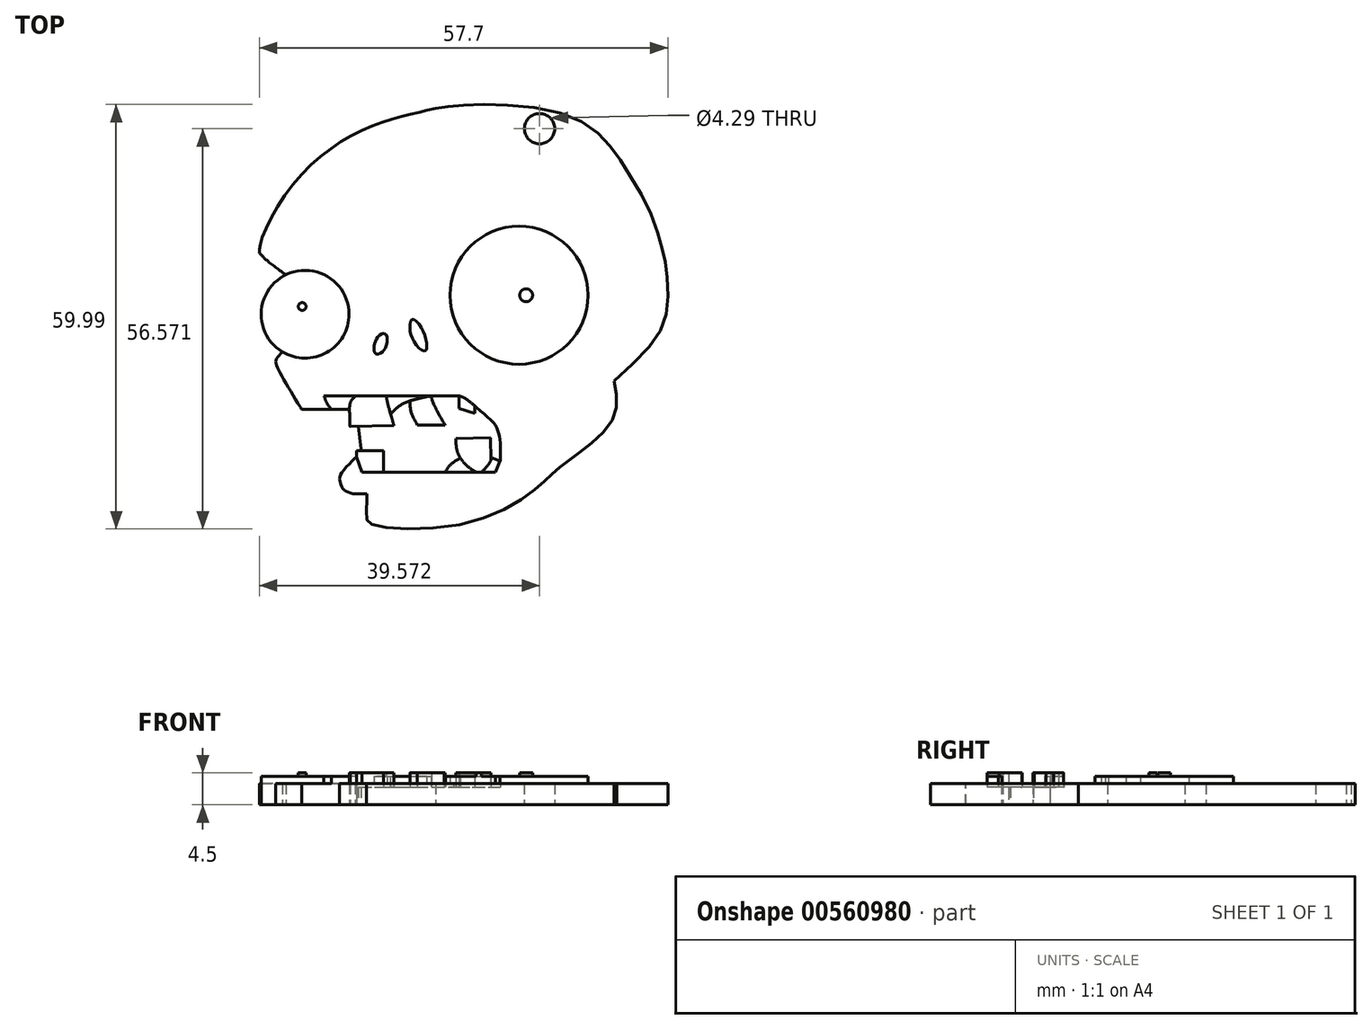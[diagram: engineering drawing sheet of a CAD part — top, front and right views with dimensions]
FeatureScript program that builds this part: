
annotation { "Feature Type Name" : "Feature", "Feature Type Description" : "" }
export const myFeature = defineFeature(function(context is Context, id is Id, definition is map)
    precondition{}
    {
        {
            var Q0;
            Q0=qCreatedBy(makeId("Top.planeOp"),FACE);
            var sketch = newSketch(context, id + "F0", { "sketchPlane" : qUnion([Q0])});
            skCircle(sketch, "E0", {"center": v(10.55, 3.84) * mm, "radius": 9.76 * mm});
            skFitSpline(sketch, "E1", {"points": [v(-1.24, 30.23) * mm, v(-6.33, 29.03) * mm, v(-13.62, 26.14) * mm, v(-21.9, 18.85) * mm, v(-26, 11.16) * mm, v(-26.1, 9.77) * mm], "startDerivative": vector(-26.84, -5.7) * mm, "endDerivative": vector(0.99, -11.94) * mm});
            skFitSpline(sketch, "E2", {"points": [v(-1.24, 30.23) * mm, v(1.46, 30.62) * mm, v(7.78, 30.76) * mm, v(17.95, 29.1) * mm, v(22.92, 25.53) * mm, v(25.72, 21.6) * mm, v(29.16, 15.43) * mm, v(30.75, 10.4) * mm, v(31.36, 7.6) * mm, v(31.5, 2.45) * mm, v(29.95, -2.13) * mm, v(23.95, -8.27) * mm], "startDerivative": vector(39.01, 6.86) * mm, "endDerivative": vector(-62.58, -55.62) * mm});
            skFitSpline(sketch, "E3", {"points": [v(23.95, -8.27) * mm, v(23.95, -13.29) * mm, v(19.3, -18.23) * mm, v(15.84, -20.84) * mm, v(13.3, -23.17) * mm, v(3.06, -28.39) * mm, v(-10.49, -28.46) * mm, v(-10.98, -27.33) * mm, v(-10.95, -24.36) * mm, v(-10.95, -24.15) * mm], "startDerivative": vector(8.57, -43.63) * mm, "endDerivative": vector(-0.07, 5.38) * mm});
            skFitSpline(sketch, "E4", {"points": [v(-10.95, -24.2) * mm, v(-12.88, -24.2) * mm, v(-14.3, -23.56) * mm, v(-14.7, -22.64) * mm, v(-14.75, -21.75) * mm, v(-12.59, -19.14) * mm], "startDerivative": vector(-8.99, -0.7) * mm, "endDerivative": vector(10.21, 10.19) * mm});
            skCircle(sketch, "E5", {"center": v(-19.68, 1.16) * mm, "radius": 6.2 * mm});
            skFitSpline(sketch, "E6", {"points": [v(-26.1, 9.77) * mm, v(-25.04, 8.74) * mm, v(-22.4, 6.73) * mm], "startDerivative": vector(2.28, -2.41) * mm, "endDerivative": vector(4.94, -3.58) * mm});
            skFitSpline(sketch, "E7", {"points": [v(-22.87, -4.17) * mm, v(-23.73, -5.16) * mm, v(-23.75, -5.96) * mm, v(-22.45, -8.5) * mm, v(-20.25, -12.15) * mm, v(-20.14, -12.3) * mm], "startDerivative": vector(-5.77, -5.5) * mm, "endDerivative": vector(1.02, -1.28) * mm});
            skLineSegment(sketch, "E8", {"start": v(-20.14, -12.3) * mm, "end": v(-15.94, -12.3) * mm});
            skFitSpline(sketch, "E9", {"points": [v(-12.5, -10.36) * mm, v(-13.26, -11.26) * mm, v(-13.38, -12.96) * mm, v(-13.31, -14.7) * mm, v(-13.3, -14.7) * mm], "startDerivative": vector(-3.23, -2.9) * mm, "endDerivative": vector(0.53, 0.26) * mm});
            skLineSegment(sketch, "E10", {"start": v(-13.3, -14.7) * mm, "end": v(-7.12, -14.56) * mm});
            skLineSegment(sketch, "E11", {"start": v(-12.5, -10.36) * mm, "end": v(-8.21, -10.36) * mm});
            skFitSpline(sketch, "E12", {"points": [v(-8.21, -10.36) * mm, v(-7.98, -11.5) * mm, v(-7.12, -14.56) * mm], "startDerivative": vector(0.46, -2.68) * mm, "endDerivative": vector(1.63, -5.49) * mm});
            skFitSpline(sketch, "E13", {"points": [v(-15.94, -12.3) * mm, v(-16.54, -11.5) * mm, v(-17.02, -10.36) * mm], "startDerivative": vector(-1.36, 1.54) * mm, "endDerivative": vector(-0.8, 2.3) * mm});
            skLineSegment(sketch, "E14", {"start": v(-17.02, -10.36) * mm, "end": v(-12.5, -10.36) * mm});
            skLineSegment(sketch, "E15", {"start": v(-15.94, -12.3) * mm, "end": v(-13.4, -12.3) * mm});
            skLineSegment(sketch, "E16", {"start": v(-8.21, -10.36) * mm, "end": v(-1.77, -10.36) * mm});
            skFitSpline(sketch, "E17", {"points": [v(-7.59, -12.96) * mm, v(-5.88, -11.5) * mm, v(-1.77, -10.36) * mm], "startDerivative": vector(3.41, 3.77) * mm, "endDerivative": vector(7.97, 1.55) * mm});
            skLineSegment(sketch, "E18", {"start": v(-3.8, -14.5) * mm, "end": v(0, -14.5) * mm});
            skLineSegment(sketch, "E19", {"start": v(0, -14.5) * mm, "end": v(0.1, -14.54) * mm});
            skFitSpline(sketch, "E20", {"points": [v(-4.86, -11.08) * mm, v(-4.71, -12.6) * mm, v(-3.8, -14.5) * mm], "startDerivative": vector(0, -3.23) * mm, "endDerivative": vector(2.04, -3.57) * mm});
            skFitSpline(sketch, "E21", {"points": [v(-1.77, -10.36) * mm, v(-1.77, -10.82) * mm, v(0.1, -14.54) * mm], "startDerivative": vector(-0.3, -1.44) * mm, "endDerivative": vector(3.42, -6.13) * mm});
            skLineSegment(sketch, "E22", {"start": v(2.07, -10.66) * mm, "end": v(2.07, -12.17) * mm});
            skLineSegment(sketch, "E23", {"start": v(2.07, -12.17) * mm, "end": v(1.98, -12.17) * mm});
            skLineSegment(sketch, "E24", {"start": v(4.28, -11.78) * mm, "end": v(4.28, -12.88) * mm});
            skLineSegment(sketch, "E25", {"start": v(2.07, -12.17) * mm, "end": v(4.28, -12.88) * mm});
            skLineSegment(sketch, "E26", {"start": v(-1.77, -10.36) * mm, "end": v(1.33, -10.36) * mm});
            skFitSpline(sketch, "E27", {"points": [v(1.33, -10.36) * mm, v(2.45, -10.5) * mm, v(4.28, -11.78) * mm], "startDerivative": vector(2.61, 0.08) * mm, "endDerivative": vector(3.26, -2.76) * mm});
            skLineSegment(sketch, "E28", {"start": v(2.07, -10.66) * mm, "end": v(2.07, -10.39) * mm});
            skFitSpline(sketch, "E29", {"points": [v(-4.58, 0.44) * mm, v(-3.8, 0) * mm, v(-2.71, -1.93) * mm, v(-2.49, -3.58) * mm, v(-2.69, -3.98) * mm, v(-3.36, -3.85) * mm, v(-4.53, -2.13) * mm, v(-4.88, -0.86) * mm, v(-4.58, 0.44) * mm]});
            skFitSpline(sketch, "E30", {"points": [v(-9.62, -2.38) * mm, v(-8.97, -1.68) * mm, v(-8.52, -1.55) * mm, v(-8.17, -1.8) * mm, v(-8.1, -2.78) * mm, v(-8.45, -3.85) * mm, v(-9.07, -4.37) * mm, v(-9.65, -4.45) * mm, v(-9.92, -3.95) * mm, v(-9.87, -3.18) * mm, v(-9.62, -2.38) * mm]});
            skFitSpline(sketch, "E31", {"points": [v(-12.15, -14.68) * mm, v(-11.76, -17.9) * mm], "startDerivative": vector(0.39, -3.22) * mm, "endDerivative": vector(0.39, -3.22) * mm});
            skLineSegment(sketch, "E32", {"start": v(-12.01, -21.18) * mm, "end": v(7.22, -21.18) * mm});
            skLineSegment(sketch, "E33", {"start": v(1.61, -16.41) * mm, "end": v(6.5, -16.26) * mm});
            skLineSegment(sketch, "E34", {"start": v(6.5, -16.26) * mm, "end": v(6.6, -19.46) * mm});
            skFitSpline(sketch, "E35", {"points": [v(1.61, -16.41) * mm, v(1.89, -18.38) * mm, v(3.09, -20.16) * mm, v(4.51, -21.18) * mm], "startDerivative": vector(0.2, -5.94) * mm, "endDerivative": vector(4.63, -2.79) * mm});
            skFitSpline(sketch, "E36", {"points": [v(6.6, -19.46) * mm, v(6.11, -20.24) * mm, v(5.24, -21.18) * mm], "startDerivative": vector(-0.93, -1.68) * mm, "endDerivative": vector(-1.76, -1.74) * mm});
            skFitSpline(sketch, "E37", {"points": [v(2.27, -19.16) * mm, v(0.83, -20.15) * mm, v(0.15, -21.18) * mm], "startDerivative": vector(-2.96, -1.7) * mm, "endDerivative": vector(-1.23, -2.35) * mm});
            skFitSpline(sketch, "E38", {"points": [v(6.59, -19.1) * mm, v(7.66, -19.51) * mm, v(7.9, -19.62) * mm], "startDerivative": vector(1.87, -0.72) * mm, "endDerivative": vector(0.63, -0.27) * mm});
            skLineSegment(sketch, "E39", {"start": v(-11.76, -17.9) * mm, "end": v(-11.76, -18.13) * mm});
            skLineSegment(sketch, "E40", {"start": v(-11.76, -18.13) * mm, "end": v(-8.63, -18.13) * mm});
            skLineSegment(sketch, "E41", {"start": v(-8.63, -18.13) * mm, "end": v(-8.63, -21.18) * mm});
            skLineSegment(sketch, "E42", {"start": v(-11.76, -18.13) * mm, "end": v(-12.42, -18.13) * mm});
            skLineSegment(sketch, "E43", {"start": v(-12.42, -18.13) * mm, "end": v(-12.42, -19) * mm});
            skLineSegment(sketch, "E44", {"start": v(-12.42, -19) * mm, "end": v(-12.59, -19.14) * mm});
            skLineSegment(sketch, "E45", {"start": v(-12.42, -19) * mm, "end": v(-11.62, -21.18) * mm});
            skFitSpline(sketch, "E46", {"points": [v(4.28, -11.78) * mm, v(5.6, -12.93) * mm, v(7.46, -15.02) * mm, v(7.9, -19.62) * mm], "startDerivative": vector(4.72, -4.24) * mm, "endDerivative": vector(-0.38, -12.2) * mm});
            skFitSpline(sketch, "E47", {"points": [v(7.22, -21.18) * mm, v(7.84, -19.59) * mm], "startDerivative": vector(0.62, 1.6) * mm, "endDerivative": vector(0.62, 1.6) * mm});
            skCircle(sketch, "E48", {"center": v(-20.09, 2.25) * mm, "radius": 0.55 * mm});
            skCircle(sketch, "E49", {"center": v(11.55, 3.84) * mm, "radius": 0.91 * mm});
            skCircle(sketch, "E50", {"center": v(13.45, 27.38) * mm, "radius": 2.14 * mm});
            skSolve(sketch);
        }
        {
            var Q0;
            Q0=makeQuery(id+"F0.imprint","IMPRINT",FACE,{"disambiguationData":[TD([[makeQuery(id+"F0.imprint","IMPRINT",EDGE,{"derivedFrom":sQuery(id+"F0.wireOp",EDGE,"E0")}),-1.0]])]});
            extrude(context, id + "F1", {"entities" : qUnion([Q0]), "depth" : 3 * mm, "offsetDistance" : 25 * mm});
        }
        {
            var Q0;
            Q0=makeQuery(id+"F0.imprint","IMPRINT",FACE,{"disambiguationData":[TD([[makeQuery(id+"F0.imprint","IMPRINT",EDGE,{"derivedFrom":sQuery(id+"F0.wireOp",EDGE,"E13")}),-1.0]])]});
            var Q1;
            {var subQ0=sQuery(id+"F0.wireOp",EDGE,"E16");Q1=makeQuery(id+"F0.imprint","IMPRINT",FACE,{"disambiguationData":[TD([[makeQuery(id+"F0.imprint","IMPRINT",EDGE,{"derivedFrom":subQ0}),-1.0]])]});}
            var Q2;
            {var subQ3=sQuery(id+"F0.wireOp",EDGE,"E37");Q2=makeQuery(id+"F0.imprint","IMPRINT",FACE,{"disambiguationData":[TD([[makeQuery(id+"F0.imprint","IMPRINT",EDGE,{"derivedFrom":subQ3}),1.0]])]});}
            var Q3;
            {var subQ0=sQuery(id+"F0.wireOp",EDGE,"E36");Q3=makeQuery(id+"F0.imprint","IMPRINT",FACE,{"disambiguationData":[TD([[makeQuery(id+"F0.imprint","IMPRINT",EDGE,{"derivedFrom":subQ0}),1.0]])]});}
            var Q4;
            Q4=makeQuery(id+"F0.imprint","IMPRINT",FACE,{"disambiguationData":[TD([[makeQuery(id+"F0.imprint","IMPRINT",EDGE,{"derivedFrom":sQuery(id+"F0.wireOp",EDGE,"E48")}),-1.0]])]});
            var Q5;
            Q5=makeQuery(id+"F0.imprint","IMPRINT",FACE,{"disambiguationData":[TD([[makeQuery(id+"F0.imprint","IMPRINT",EDGE,{"derivedFrom":sQuery(id+"F0.wireOp",EDGE,"E0")}),1.0]])]});
            var Q6;
            Q6=makeQuery(id+"F0.imprint","IMPRINT",FACE,{"disambiguationData":[TD([[makeQuery(id+"F0.imprint","IMPRINT",EDGE,{"derivedFrom":sQuery(id+"F0.wireOp",EDGE,"E29")}),-1.0]])]});
            var Q7;
            Q7=makeQuery(id+"F0.imprint","IMPRINT",FACE,{"disambiguationData":[TD([[makeQuery(id+"F0.imprint","IMPRINT",EDGE,{"derivedFrom":sQuery(id+"F0.wireOp",EDGE,"E30")}),-1.0]])]});
            extrude(context, id + "F2", {"entities" : qUnion([Q0, Q1, Q2, Q3, Q4, Q5, Q6, Q7]), "operationType" : NewBodyOperationType.ADD, "depth" : 4 * mm, "offsetDistance" : 25 * mm});
        }
        {
            var Q0;
            {var subQ7=sQuery(id+"F0.wireOp",EDGE,"E11");Q0=makeQuery(id+"F0.imprint","IMPRINT",FACE,{"disambiguationData":[TD([[makeQuery(id+"F0.imprint","IMPRINT",EDGE,{"derivedFrom":subQ7}),-1.0]])]});}
            var Q1;
            Q1=makeQuery(id+"F0.imprint","IMPRINT",FACE,{"disambiguationData":[TD([[makeQuery(id+"F0.imprint","IMPRINT",EDGE,{"derivedFrom":sQuery(id+"F0.wireOp",EDGE,"E18")}),1.0]])]});
            var Q2;
            Q2=makeQuery(id+"F0.imprint","IMPRINT",FACE,{"disambiguationData":[TD([[makeQuery(id+"F0.imprint","IMPRINT",EDGE,{"derivedFrom":sQuery(id+"F0.wireOp",EDGE,"E22")}),1.0]])]});
            var Q3;
            {var subQ3=sQuery(id+"F0.wireOp",EDGE,"E33");Q3=makeQuery(id+"F0.imprint","IMPRINT",FACE,{"disambiguationData":[TD([[makeQuery(id+"F0.imprint","IMPRINT",EDGE,{"derivedFrom":subQ3}),-1.0]])]});}
            var Q4;
            Q4=makeQuery(id+"F0.imprint","IMPRINT",FACE,{"disambiguationData":[TD([[makeQuery(id+"F0.imprint","IMPRINT",EDGE,{"derivedFrom":sQuery(id+"F0.wireOp",EDGE,"E40")}),-1.0]])]});
            extrude(context, id + "F3", {"entities" : qUnion([Q0, Q1, Q2, Q3, Q4]), "operationType" : NewBodyOperationType.ADD, "depth" : 4.5 * mm, "offsetDistance" : 25 * mm});
        }
        {
            var Q0;
            Q0=makeQuery(id+"F0.imprint","IMPRINT",FACE,{"disambiguationData":[TD([[makeQuery(id+"F0.imprint","IMPRINT",EDGE,{"derivedFrom":sQuery(id+"F0.wireOp",EDGE,"E48")}),1.0]])]});
            var Q1;
            Q1=makeQuery(id+"F0.imprint","IMPRINT",FACE,{"disambiguationData":[TD([[makeQuery(id+"F0.imprint","IMPRINT",EDGE,{"derivedFrom":sQuery(id+"F0.wireOp",EDGE,"E49")}),1.0]])]});
            extrude(context, id + "F4", {"entities" : qUnion([Q0, Q1]), "operationType" : NewBodyOperationType.ADD, "depth" : 4.5 * mm, "offsetDistance" : 25 * mm});
        }
        {
            var Q0;
            Q0=makeQuery(id+"F0.imprint","IMPRINT",FACE,{"disambiguationData":[TD([[makeQuery(id+"F0.imprint","IMPRINT",EDGE,{"derivedFrom":sQuery(id+"F0.wireOp",EDGE,"E18")}),-1.0]])]});
            extrude(context, id + "F5", {"entities" : qUnion([Q0]), "operationType" : NewBodyOperationType.ADD, "depth" : 2.5 * mm, "offsetDistance" : 25 * mm});
        }
    });
